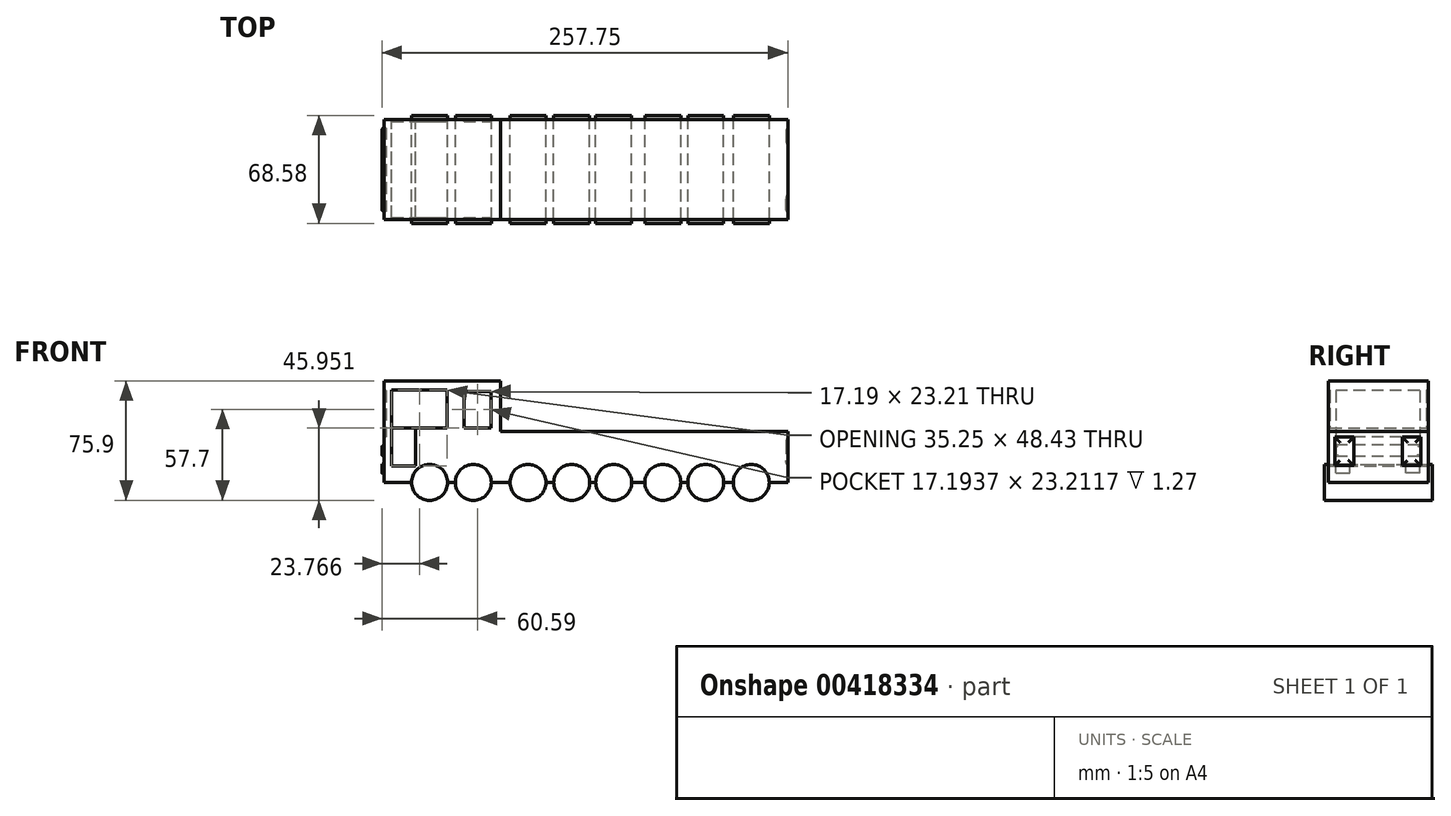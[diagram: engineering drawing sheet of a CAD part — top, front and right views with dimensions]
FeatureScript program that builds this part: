
annotation { "Feature Type Name" : "Feature", "Feature Type Description" : "" }
export const myFeature = defineFeature(function(context is Context, id is Id, definition is map)
    precondition{}
    {
        {
            var Q0;
            Q0=qCreatedBy(makeId("Front.planeOp"),FACE);
            var sketch = newSketch(context, id + "F0", { "sketchPlane" : qUnion([Q0])});
            skLineSegment(sketch, "E0.bottom", {"start": v(-132.68, 35.68) * mm, "end": v(-58.75, 35.68) * mm});
            skLineSegment(sketch, "E0.top", {"start": v(-132.68, -28.8) * mm, "end": v(-115.16, -28.8) * mm});
            skLineSegment(sketch, "E0.left", {"start": v(-132.68, 35.68) * mm, "end": v(-132.68, -28.8) * mm});
            skLineSegment(sketch, "E0.right", {"start": v(-58.75, 35.68) * mm, "end": v(-58.75, -28.8) * mm});
            skLineSegment(sketch, "E1.bottom", {"start": v(-58.75, 3.44) * mm, "end": v(123.8, 3.44) * mm});
            skLineSegment(sketch, "E1.top", {"start": v(-58.75, -28.8) * mm, "end": v(-52.68, -28.8) * mm});
            skLineSegment(sketch, "E1.left", {"start": v(-58.75, 3.44) * mm, "end": v(-58.75, -28.8) * mm});
            skLineSegment(sketch, "E1.right", {"start": v(123.8, 3.44) * mm, "end": v(123.8, -28.8) * mm});
            skCircle(sketch, "E2", {"center": v(-103.74, -28.8) * mm, "radius": 11.42 * mm});
            skCircle(sketch, "E3", {"center": v(-75.94, -28.8) * mm, "radius": 11.42 * mm});
            skCircle(sketch, "E4", {"center": v(-41.27, -28.8) * mm, "radius": 11.42 * mm});
            skCircle(sketch, "E5", {"center": v(-13.47, -28.8) * mm, "radius": 11.42 * mm});
            skCircle(sketch, "E6", {"center": v(13.18, -28.8) * mm, "radius": 11.42 * mm});
            skCircle(sketch, "E7", {"center": v(44.42, -28.8) * mm, "radius": 11.42 * mm});
            skCircle(sketch, "E8", {"center": v(71.64, -28.8) * mm, "radius": 11.42 * mm});
            skCircle(sketch, "E9", {"center": v(100.58, -28.8) * mm, "radius": 11.42 * mm});
            skLineSegment(sketch, "E10.bottom", {"start": v(-127.8, 29.95) * mm, "end": v(-92.56, 29.95) * mm});
            skLineSegment(sketch, "E10.top", {"start": v(-127.8, 5.87) * mm, "end": v(-92.56, 5.87) * mm});
            skLineSegment(sketch, "E10.left", {"start": v(-127.8, 29.95) * mm, "end": v(-127.8, 5.87) * mm});
            skLineSegment(sketch, "E10.right", {"start": v(-92.56, 29.95) * mm, "end": v(-92.56, 5.87) * mm});
            skLineSegment(sketch, "E11.bottom", {"start": v(-81.96, 29.09) * mm, "end": v(-64.76, 29.09) * mm});
            skLineSegment(sketch, "E11.top", {"start": v(-81.96, 5.87) * mm, "end": v(-64.76, 5.87) * mm});
            skLineSegment(sketch, "E11.left", {"start": v(-81.96, 29.09) * mm, "end": v(-81.96, 5.87) * mm});
            skLineSegment(sketch, "E11.right", {"start": v(-64.76, 29.09) * mm, "end": v(-64.76, 5.87) * mm});
            skLineSegment(sketch, "E12.bottom", {"start": v(-112.62, 5.87) * mm, "end": v(-127.8, 5.87) * mm});
            skLineSegment(sketch, "E12.top", {"start": v(-112.62, -18.48) * mm, "end": v(-127.8, -18.48) * mm});
            skLineSegment(sketch, "E12.left", {"start": v(-112.62, 5.87) * mm, "end": v(-112.62, -18.48) * mm});
            skLineSegment(sketch, "E12.right", {"start": v(-127.8, 5.87) * mm, "end": v(-127.8, -18.48) * mm});
            skLineSegment(sketch, "E13.trimOffspring", {"start": v(-92.32, -28.8) * mm, "end": v(-87.36, -28.8) * mm});
            skLineSegment(sketch, "E14.trimOffspring", {"start": v(-64.52, -28.8) * mm, "end": v(-58.75, -28.8) * mm});
            skLineSegment(sketch, "E15.trimOffspring", {"start": v(-29.85, -28.8) * mm, "end": v(-24.89, -28.8) * mm});
            skLineSegment(sketch, "E16.trimOffspring", {"start": v(-2.05, -28.8) * mm, "end": v(1.76, -28.8) * mm});
            skLineSegment(sketch, "E17.trimOffspring", {"start": v(24.6, -28.8) * mm, "end": v(33, -28.8) * mm});
            skLineSegment(sketch, "E18.trimOffspring", {"start": v(55.84, -28.8) * mm, "end": v(60.22, -28.8) * mm});
            skLineSegment(sketch, "E19.trimOffspring", {"start": v(83.06, -28.8) * mm, "end": v(89.16, -28.8) * mm});
            skLineSegment(sketch, "E20.trimOffspring", {"start": v(112, -28.8) * mm, "end": v(123.8, -28.8) * mm});
            skSolve(sketch);
        }
        {
            var Q0;
            Q0=makeQuery(id+"F0.imprint","IMPRINT",FACE,{"disambiguationData":[TD([[makeQuery(id+"F0.imprint","IMPRINT",EDGE,{"derivedFrom":sQuery(id+"F0.wireOp",EDGE,"E0.bottom")}),-1.0]])]});
            var Q1;
            Q1=makeQuery(id+"F0.imprint","IMPRINT",FACE,{"disambiguationData":[TD([[makeQuery(id+"F0.imprint","IMPRINT",EDGE,{"derivedFrom":sQuery(id+"F0.wireOp",EDGE,"E1.bottom")}),-1.0]])]});
            extrude(context, id + "F1", {"entities" : qUnion([Q0, Q1]), "endBound" : BoundingType.SYMMETRIC, "depth" : 63.5 * mm});
        }
        {
            var Q0;
            Q0=makeQuery(id+"F1.opExtrude","SWEPT_FACE",FACE,{"disambiguationData":[OSD([sQuery(id+"F0.wireOp",EDGE,"E0.left")])]});
            var sketch = newSketch(context, id + "F2", { "sketchPlane" : qUnion([Q0])});
            skLineSegment(sketch, "E21.bottom", {"start": v(-26.39, 29.52) * mm, "end": v(26.73, 29.52) * mm});
            skLineSegment(sketch, "E21.top", {"start": v(-26.39, 0) * mm, "end": v(26.73, 0) * mm});
            skLineSegment(sketch, "E21.left", {"start": v(-26.39, 29.52) * mm, "end": v(-26.39, 0) * mm});
            skLineSegment(sketch, "E21.right", {"start": v(26.73, 29.52) * mm, "end": v(26.73, 0) * mm});
            skLineSegment(sketch, "E22.bottom", {"start": v(-26.39, -5.14) * mm, "end": v(26.73, -5.14) * mm});
            skLineSegment(sketch, "E22.top", {"start": v(-26.39, -12.35) * mm, "end": v(26.73, -12.35) * mm});
            skLineSegment(sketch, "E22.left", {"start": v(-26.39, -5.14) * mm, "end": v(-26.39, -12.35) * mm});
            skLineSegment(sketch, "E22.right", {"start": v(26.73, -5.14) * mm, "end": v(26.73, -12.35) * mm});
            skLineSegment(sketch, "E23.bottom", {"start": v(-26.39, -22.7) * mm, "end": v(-17.54, -22.7) * mm});
            skLineSegment(sketch, "E23.top", {"start": v(-26.39, -17.16) * mm, "end": v(-17.54, -17.16) * mm});
            skLineSegment(sketch, "E23.left", {"start": v(-26.39, -22.7) * mm, "end": v(-26.39, -17.16) * mm});
            skLineSegment(sketch, "E23.right", {"start": v(-17.54, -22.7) * mm, "end": v(-17.54, -17.16) * mm});
            skLineSegment(sketch, "E24.bottom", {"start": v(26.73, -22.95) * mm, "end": v(17.88, -22.95) * mm});
            skLineSegment(sketch, "E24.top", {"start": v(26.73, -17.16) * mm, "end": v(17.88, -17.16) * mm});
            skLineSegment(sketch, "E24.left", {"start": v(26.73, -22.95) * mm, "end": v(26.73, -17.16) * mm});
            skLineSegment(sketch, "E24.right", {"start": v(17.88, -22.95) * mm, "end": v(17.88, -17.16) * mm});
            skSolve(sketch);
        }
        {
            var Q0;
            Q0=makeQuery(id+"F2.imprint","IMPRINT",FACE,{"disambiguationData":[TD([[makeQuery(id+"F2.imprint","IMPRINT",EDGE,{"derivedFrom":sQuery(id+"F2.wireOp",EDGE,"E23.bottom")}),1.0]])]});
            var Q1;
            Q1=makeQuery(id+"F2.imprint","IMPRINT",FACE,{"disambiguationData":[TD([[makeQuery(id+"F2.imprint","IMPRINT",EDGE,{"derivedFrom":sQuery(id+"F2.wireOp",EDGE,"E24.bottom")}),-1.0]])]});
            var Q2;
            Q2=makeQuery(id+"F2.imprint","IMPRINT",FACE,{"disambiguationData":[TD([[makeQuery(id+"F2.imprint","IMPRINT",EDGE,{"derivedFrom":sQuery(id+"F2.wireOp",EDGE,"E22.bottom")}),-1.0]])]});
            extrude(context, id + "F3", {"entities" : qUnion([Q0, Q1, Q2]), "operationType" : NewBodyOperationType.ADD, "depth" : 1.27 * mm});
        }
        {
            var Q0;
            Q0=makeQuery(id+"F2.imprint","IMPRINT",FACE,{"disambiguationData":[TD([[makeQuery(id+"F2.imprint","IMPRINT",EDGE,{"derivedFrom":sQuery(id+"F2.wireOp",EDGE,"E21.bottom")}),-1.0]])]});
            extrude(context, id + "F4", {"entities" : qUnion([Q0]), "operationType" : NewBodyOperationType.REMOVE, "oppositeDirection" : true, "depth" : 1.27 * mm});
        }
        {
            var Q0;
            Q0=makeQuery(id+"F3.opExtrude","CAP_EDGE",EDGE,{"disambiguationData":[OSD([sQuery(id+"F2.wireOp",EDGE,"E23.right")])],"isStart":false});
            var Q1;
            Q1=makeQuery(id+"F3.opExtrude","CAP_EDGE",EDGE,{"disambiguationData":[OSD([sQuery(id+"F2.wireOp",EDGE,"E24.left")])],"isStart":false});
            var Q2;
            Q2=makeQuery(id+"F3.opExtrude","CAP_EDGE",EDGE,{"disambiguationData":[OSD([sQuery(id+"F2.wireOp",EDGE,"E23.left")])],"isStart":false});
            var Q3;
            Q3=makeQuery(id+"F3.opExtrude","CAP_EDGE",EDGE,{"disambiguationData":[OSD([sQuery(id+"F2.wireOp",EDGE,"E24.right")])],"isStart":false});
            fillet(context, id + "F5", {"entities" : qUnion([Q0, Q1, Q2, Q3]), "radius" : 5.08 * mm, "tangentPropagation" : true, "allowEdgeOverflow" : false});
        }
        {
            var Q0;
            Q0=makeQuery(id+"F3.opExtrude","CAP_EDGE",EDGE,{"disambiguationData":[OSD([sQuery(id+"F2.wireOp",EDGE,"E22.top")])],"isStart":false});
            var Q1;
            Q1=makeQuery(id+"F3.opExtrude","CAP_EDGE",EDGE,{"disambiguationData":[OSD([sQuery(id+"F2.wireOp",EDGE,"E22.left")])],"isStart":false});
            var Q2;
            Q2=makeQuery(id+"F3.opExtrude","CAP_EDGE",EDGE,{"disambiguationData":[OSD([sQuery(id+"F2.wireOp",EDGE,"E22.bottom")])],"isStart":false});
            var Q3;
            Q3=makeQuery(id+"F3.opExtrude","CAP_EDGE",EDGE,{"disambiguationData":[OSD([sQuery(id+"F2.wireOp",EDGE,"E22.right")])],"isStart":false});
            fillet(context, id + "F6", {"entities" : qUnion([Q0, Q1, Q2, Q3]), "radius" : 1.27 * mm, "tangentPropagation" : true, "allowEdgeOverflow" : false});
        }
        {
            var Q0;
            {var subQ0=sQuery(id+"F0.wireOp",EDGE,"E2");var subQ1=makeQuery(id+"F0.imprint","INTERSECT",VERTEX,{"derivedFrom":[sQuery(id+"F0.wireOp",EDGE,"E0.top"),subQ0]});Q0=makeQuery(id+"F0.imprint","IMPRINT",FACE,{"disambiguationData":[TD([[makeQuery(id+"F0.imprint","IMPRINT",EDGE,{"disambiguationData":[TD([[subQ1,1.0]])],"derivedFrom":subQ0}),1.0]])]});}
            var Q1;
            {var subQ0=sQuery(id+"F0.wireOp",EDGE,"E3");var subQ1=makeQuery(id+"F0.imprint","INTERSECT",VERTEX,{"derivedFrom":[subQ0,sQuery(id+"F0.wireOp",EDGE,"E13.trimOffspring")]});Q1=makeQuery(id+"F0.imprint","IMPRINT",FACE,{"disambiguationData":[TD([[makeQuery(id+"F0.imprint","IMPRINT",EDGE,{"disambiguationData":[TD([[subQ1,1.0]])],"derivedFrom":subQ0}),1.0]])]});}
            var Q2;
            {var subQ0=sQuery(id+"F0.wireOp",EDGE,"E4");var subQ1=makeQuery(id+"F0.imprint","INTERSECT",VERTEX,{"derivedFrom":[sQuery(id+"F0.wireOp",EDGE,"E1.top"),subQ0]});Q2=makeQuery(id+"F0.imprint","IMPRINT",FACE,{"disambiguationData":[TD([[makeQuery(id+"F0.imprint","IMPRINT",EDGE,{"disambiguationData":[TD([[subQ1,1.0]])],"derivedFrom":subQ0}),1.0]])]});}
            var Q3;
            {var subQ0=sQuery(id+"F0.wireOp",EDGE,"E5");var subQ1=makeQuery(id+"F0.imprint","INTERSECT",VERTEX,{"derivedFrom":[subQ0,sQuery(id+"F0.wireOp",EDGE,"E15.trimOffspring")]});Q3=makeQuery(id+"F0.imprint","IMPRINT",FACE,{"disambiguationData":[TD([[makeQuery(id+"F0.imprint","IMPRINT",EDGE,{"disambiguationData":[TD([[subQ1,1.0]])],"derivedFrom":subQ0}),1.0]])]});}
            var Q4;
            {var subQ0=sQuery(id+"F0.wireOp",EDGE,"E6");var subQ1=makeQuery(id+"F0.imprint","INTERSECT",VERTEX,{"derivedFrom":[subQ0,sQuery(id+"F0.wireOp",EDGE,"E16.trimOffspring")]});Q4=makeQuery(id+"F0.imprint","IMPRINT",FACE,{"disambiguationData":[TD([[makeQuery(id+"F0.imprint","IMPRINT",EDGE,{"disambiguationData":[TD([[subQ1,1.0]])],"derivedFrom":subQ0}),1.0]])]});}
            var Q5;
            {var subQ0=sQuery(id+"F0.wireOp",EDGE,"E7");var subQ1=makeQuery(id+"F0.imprint","INTERSECT",VERTEX,{"derivedFrom":[subQ0,sQuery(id+"F0.wireOp",EDGE,"E17.trimOffspring")]});Q5=makeQuery(id+"F0.imprint","IMPRINT",FACE,{"disambiguationData":[TD([[makeQuery(id+"F0.imprint","IMPRINT",EDGE,{"disambiguationData":[TD([[subQ1,1.0]])],"derivedFrom":subQ0}),1.0]])]});}
            var Q6;
            {var subQ0=sQuery(id+"F0.wireOp",EDGE,"E8");var subQ1=makeQuery(id+"F0.imprint","INTERSECT",VERTEX,{"derivedFrom":[subQ0,sQuery(id+"F0.wireOp",EDGE,"E18.trimOffspring")]});Q6=makeQuery(id+"F0.imprint","IMPRINT",FACE,{"disambiguationData":[TD([[makeQuery(id+"F0.imprint","IMPRINT",EDGE,{"disambiguationData":[TD([[subQ1,1.0]])],"derivedFrom":subQ0}),1.0]])]});}
            var Q7;
            {var subQ0=sQuery(id+"F0.wireOp",EDGE,"E9");var subQ1=makeQuery(id+"F0.imprint","INTERSECT",VERTEX,{"derivedFrom":[subQ0,sQuery(id+"F0.wireOp",EDGE,"E19.trimOffspring")]});Q7=makeQuery(id+"F0.imprint","IMPRINT",FACE,{"disambiguationData":[TD([[makeQuery(id+"F0.imprint","IMPRINT",EDGE,{"disambiguationData":[TD([[subQ1,1.0]])],"derivedFrom":subQ0}),1.0]])]});}
            extrude(context, id + "F7", {"entities" : qUnion([Q0, Q1, Q2, Q3, Q4, Q5, Q6, Q7]), "endBound" : BoundingType.SYMMETRIC, "depth" : 68.58 * mm});
        }
        {
            var Q0;
            Q0=makeQuery(id+"F0.imprint","IMPRINT",FACE,{"disambiguationData":[TD([[makeQuery(id+"F0.imprint","IMPRINT",EDGE,{"derivedFrom":sQuery(id+"F0.wireOp",EDGE,"E10.bottom")}),-1.0]])]});
            var Q1;
            Q1=makeQuery(id+"F0.imprint","IMPRINT",FACE,{"disambiguationData":[TD([[makeQuery(id+"F0.imprint","IMPRINT",EDGE,{"derivedFrom":sQuery(id+"F0.wireOp",EDGE,"E12.bottom")}),1.0]])]});
            var Q2;
            Q2=makeQuery(id+"F0.imprint","IMPRINT",FACE,{"disambiguationData":[TD([[makeQuery(id+"F0.imprint","IMPRINT",EDGE,{"derivedFrom":sQuery(id+"F0.wireOp",EDGE,"E11.bottom")}),-1.0]])]});
            extrude(context, id + "F8", {"entities" : qUnion([Q0, Q1, Q2]), "operationType" : NewBodyOperationType.ADD, "endBound" : BoundingType.SYMMETRIC, "depth" : 60.96 * mm});
        }
        {
            var Q0;
            Q0=makeQuery(id+"F1.opExtrude","SWEPT_FACE",FACE,{"disambiguationData":[OSD([sQuery(id+"F0.wireOp",EDGE,"E1.right")])]});
            var sketch = newSketch(context, id + "F9", { "sketchPlane" : qUnion([Q0])});
            skLineSegment(sketch, "E25.bottom", {"start": v(-27.6, 0) * mm, "end": v(-15.4, 0) * mm});
            skLineSegment(sketch, "E25.top", {"start": v(-27.6, -18.16) * mm, "end": v(-15.4, -18.16) * mm});
            skLineSegment(sketch, "E25.left", {"start": v(-27.6, 0) * mm, "end": v(-27.6, -18.16) * mm});
            skLineSegment(sketch, "E25.right", {"start": v(-15.4, 0) * mm, "end": v(-15.4, -18.16) * mm});
            skLineSegment(sketch, "E26.bottom", {"start": v(27.04, 0) * mm, "end": v(15.24, 0) * mm});
            skLineSegment(sketch, "E26.top", {"start": v(27.04, -18.16) * mm, "end": v(15.24, -18.16) * mm});
            skLineSegment(sketch, "E26.left", {"start": v(27.04, 0) * mm, "end": v(27.04, -18.16) * mm});
            skLineSegment(sketch, "E26.right", {"start": v(15.24, 0) * mm, "end": v(15.24, -18.16) * mm});
            skSolve(sketch);
        }
        {
            var Q0;
            Q0=makeQuery(id+"F9.imprint","IMPRINT",FACE,{"disambiguationData":[TD([[makeQuery(id+"F9.imprint","IMPRINT",EDGE,{"derivedFrom":sQuery(id+"F9.wireOp",EDGE,"E25.bottom")}),-1.0]])]});
            var Q1;
            Q1=makeQuery(id+"F9.imprint","IMPRINT",FACE,{"disambiguationData":[TD([[makeQuery(id+"F9.imprint","IMPRINT",EDGE,{"derivedFrom":sQuery(id+"F9.wireOp",EDGE,"E26.bottom")}),1.0]])]});
            extrude(context, id + "F10", {"entities" : qUnion([Q0, Q1]), "operationType" : NewBodyOperationType.REMOVE, "oppositeDirection" : true, "depth" : 1.27 * mm});
        }
        {
            var Q0;
            Q0=makeQuery(id+"F10.boolean.opBoolean","COPY",EDGE,{"derivedFrom":makeQuery(id+"F10.opExtrude","CAP_EDGE",EDGE,{"disambiguationData":[OSD([sQuery(id+"F9.wireOp",EDGE,"E25.left")])],"isStart":false})});
            var Q1;
            Q1=makeQuery(id+"F10.boolean.opBoolean","COPY",EDGE,{"derivedFrom":makeQuery(id+"F10.opExtrude","CAP_EDGE",EDGE,{"disambiguationData":[OSD([sQuery(id+"F9.wireOp",EDGE,"E25.bottom")])],"isStart":false})});
            var Q2;
            Q2=makeQuery(id+"F10.boolean.opBoolean","COPY",EDGE,{"derivedFrom":makeQuery(id+"F10.opExtrude","CAP_EDGE",EDGE,{"disambiguationData":[OSD([sQuery(id+"F9.wireOp",EDGE,"E25.right")])],"isStart":false})});
            var Q3;
            Q3=makeQuery(id+"F10.boolean.opBoolean","COPY",EDGE,{"derivedFrom":makeQuery(id+"F10.opExtrude","CAP_EDGE",EDGE,{"disambiguationData":[OSD([sQuery(id+"F9.wireOp",EDGE,"E25.top")])],"isStart":false})});
            var Q4;
            Q4=makeQuery(id+"F10.boolean.opBoolean","COPY",EDGE,{"derivedFrom":makeQuery(id+"F10.opExtrude","CAP_EDGE",EDGE,{"disambiguationData":[OSD([sQuery(id+"F9.wireOp",EDGE,"E26.right")])],"isStart":false})});
            var Q5;
            Q5=makeQuery(id+"F10.boolean.opBoolean","COPY",EDGE,{"derivedFrom":makeQuery(id+"F10.opExtrude","CAP_EDGE",EDGE,{"disambiguationData":[OSD([sQuery(id+"F9.wireOp",EDGE,"E26.bottom")])],"isStart":false})});
            var Q6;
            Q6=makeQuery(id+"F10.boolean.opBoolean","COPY",EDGE,{"derivedFrom":makeQuery(id+"F10.opExtrude","CAP_EDGE",EDGE,{"disambiguationData":[OSD([sQuery(id+"F9.wireOp",EDGE,"E26.left")])],"isStart":false})});
            var Q7;
            Q7=makeQuery(id+"F10.boolean.opBoolean","COPY",EDGE,{"derivedFrom":makeQuery(id+"F10.opExtrude","CAP_EDGE",EDGE,{"disambiguationData":[OSD([sQuery(id+"F9.wireOp",EDGE,"E26.top")])],"isStart":false})});
            fillet(context, id + "F11", {"entities" : qUnion([Q0, Q1, Q2, Q3, Q4, Q5, Q6, Q7]), "radius" : 5.08 * mm, "tangentPropagation" : true, "allowEdgeOverflow" : false});
        }
    });
